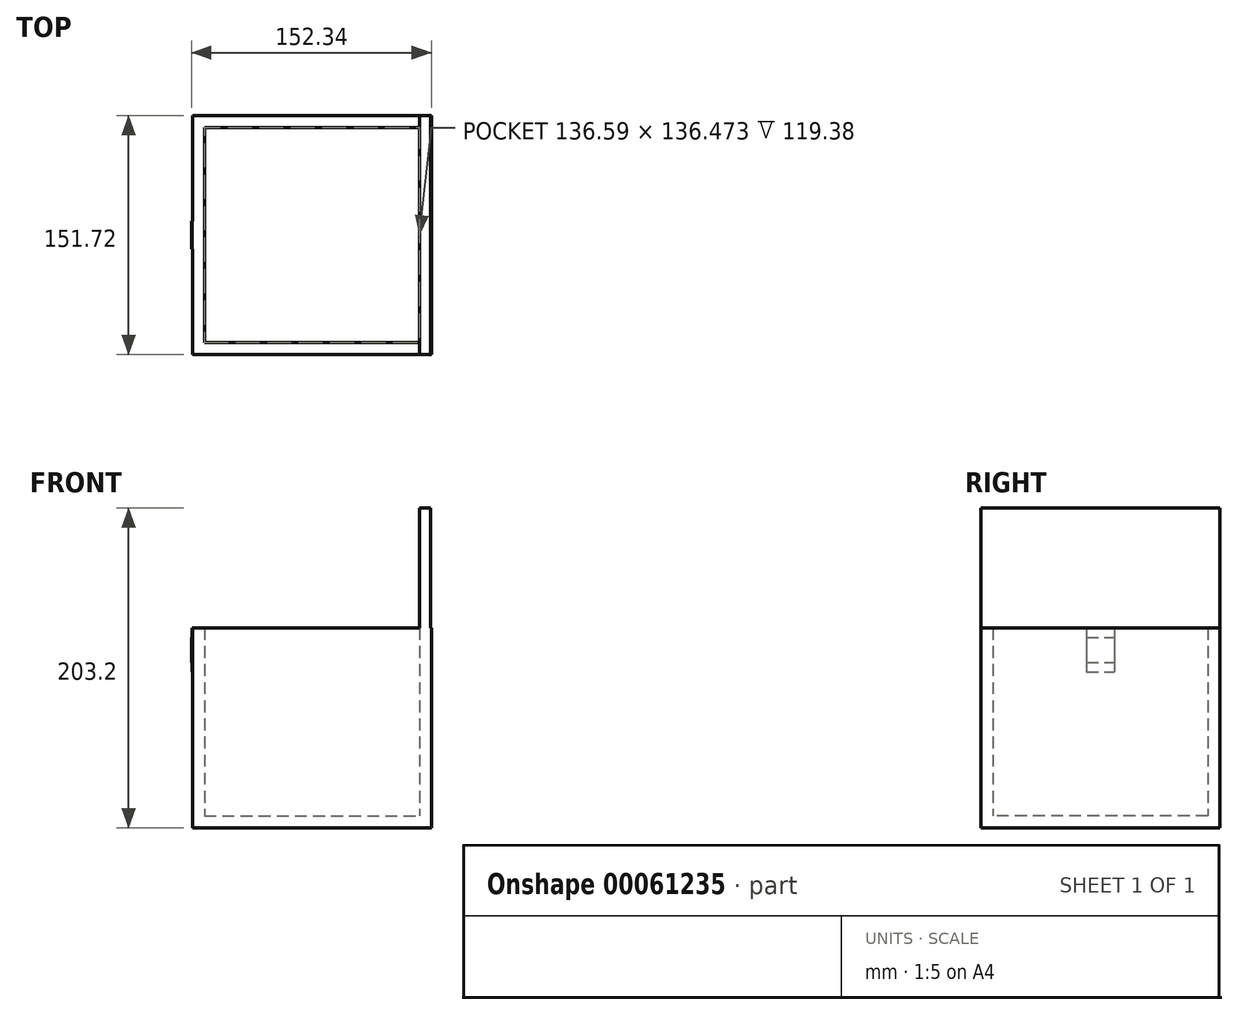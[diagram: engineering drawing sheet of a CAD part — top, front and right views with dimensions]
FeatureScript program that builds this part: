
annotation { "Feature Type Name" : "Feature", "Feature Type Description" : "" }
export const myFeature = defineFeature(function(context is Context, id is Id, definition is map)
    precondition{}
    {
        {
            var Q0;
            Q0=qCreatedBy(makeId("Top.planeOp"),FACE);
            var sketch = newSketch(context, id + "F0", { "sketchPlane" : qUnion([Q0])});
            skLineSegment(sketch, "E0.rect.bottom", {"start": v(-75.92, 75.86) * mm, "end": v(75.92, 75.86) * mm});
            skLineSegment(sketch, "E0.rect.top", {"start": v(-75.92, -75.86) * mm, "end": v(75.92, -75.86) * mm});
            skLineSegment(sketch, "E0.rect.left", {"start": v(-75.92, 75.86) * mm, "end": v(-75.92, -75.86) * mm});
            skLineSegment(sketch, "E0.rect.right", {"start": v(75.92, 75.86) * mm, "end": v(75.92, -75.86) * mm});
            skPoint(sketch, "E0.rect.middle", {"position": v(0, 0) * mm});
            skSolve(sketch);
        }
        {
            var Q0;
            Q0=makeQuery(id+"F0.imprint","IMPRINT",FACE,{"disambiguationData":[TD([[makeQuery(id+"F0.imprint","IMPRINT",EDGE,{"derivedFrom":sQuery(id+"F0.wireOp",EDGE,"E0.rect.bottom")}),-1.0]])]});
            extrude(context, id + "F1", {"entities" : qUnion([Q0]), "depth" : 127 * mm});
        }
        {
            var Q0;
            Q0=makeQuery(id+"F1.opExtrude","CAP_FACE",FACE,{"disambiguationData":[OSD([sQuery(id+"F0.wireOp",EDGE,"E0.rect.bottom"),sQuery(id+"F0.wireOp",EDGE,"E0.rect.top"),sQuery(id+"F0.wireOp",EDGE,"E0.rect.left"),sQuery(id+"F0.wireOp",EDGE,"E0.rect.right")])],"isStart":false});
            shell(context, id + "F2", {"entities" : qUnion([Q0]), "thickness" : 7.62 * mm});
        }
        {
            var Q0;
            Q0=makeQuery(id+"F1.opExtrude","CAP_FACE",FACE,{"disambiguationData":[OSD([sQuery(id+"F0.wireOp",EDGE,"E0.rect.bottom"),sQuery(id+"F0.wireOp",EDGE,"E0.rect.top"),sQuery(id+"F0.wireOp",EDGE,"E0.rect.left"),sQuery(id+"F0.wireOp",EDGE,"E0.rect.right")])],"isStart":false});
            var sketch = newSketch(context, id + "F3", { "sketchPlane" : qUnion([Q0])});
            skLineSegment(sketch, "E1.rect.bottom", {"start": v(75.24, -75.86) * mm, "end": v(68.36, -75.86) * mm});
            skLineSegment(sketch, "E1.rect.top", {"start": v(75.24, 83.18) * mm, "end": v(68.36, 83.18) * mm});
            skLineSegment(sketch, "E1.rect.left", {"start": v(75.24, -75.86) * mm, "end": v(75.24, 83.18) * mm});
            skLineSegment(sketch, "E1.rect.right", {"start": v(68.36, -75.86) * mm, "end": v(68.36, 83.18) * mm});
            skPoint(sketch, "E1.rect.middle", {"position": v(71.8, 3.66) * mm});
            skSolve(sketch);
        }
        {
            var Q0;
            {var subQ0=sQuery(id+"F3.wireOp",EDGE,"E1.rect.bottom");Q0=makeQuery(id+"F3.imprint","IMPRINT",FACE,{"disambiguationData":[TD([[makeQuery(id+"F3.imprint","IMPRINT",EDGE,{"derivedFrom":subQ0}),1.0]])]});}
            extrude(context, id + "F4", {"entities" : qUnion([Q0]), "operationType" : NewBodyOperationType.ADD, "depth" : 76.2 * mm});
        }
        {
            var Q0;
            Q0=makeQuery(id+"F1.opExtrude","SWEPT_FACE",FACE,{"disambiguationData":[OSD([sQuery(id+"F0.wireOp",EDGE,"E0.rect.left")])]});
            var sketch = newSketch(context, id + "F5", { "sketchPlane" : qUnion([Q0])});
            skLineSegment(sketch, "E2.rect.bottom", {"start": v(8.82, 127) * mm, "end": v(-8.82, 127) * mm});
            skLineSegment(sketch, "E2.rect.top", {"start": v(8.82, 99.04) * mm, "end": v(-8.82, 99.04) * mm});
            skLineSegment(sketch, "E2.rect.left", {"start": v(8.82, 127) * mm, "end": v(8.82, 99.04) * mm});
            skLineSegment(sketch, "E2.rect.right", {"start": v(-8.82, 127) * mm, "end": v(-8.82, 99.04) * mm});
            skPoint(sketch, "E2.rect.middle", {"position": v(0, 113.02) * mm});
            skPoint(sketch, "E2.rect.middle.positionSnap0", {"position": v(0, 127) * mm});
            skPoint(sketch, "E2.rect.centerSnap0", {"position": v(0, 127) * mm});
            skSolve(sketch);
        }
        {
            var Q0;
            Q0=makeQuery(id+"F5.imprint","IMPRINT",FACE,{"disambiguationData":[TD([[makeQuery(id+"F5.imprint","IMPRINT",EDGE,{"derivedFrom":sQuery(id+"F5.wireOp",EDGE,"E2.rect.bottom")}),-1.0]])]});
            extrude(context, id + "F6", {"entities" : qUnion([Q0]), "operationType" : NewBodyOperationType.ADD, "depth" : 0.25 * mm});
        }
        {
            var Q0;
            Q0=makeQuery(id+"F6.opExtrude","CAP_FACE",FACE,{"disambiguationData":[OSD([sQuery(id+"F5.wireOp",EDGE,"E2.rect.bottom"),sQuery(id+"F5.wireOp",EDGE,"E2.rect.top"),sQuery(id+"F5.wireOp",EDGE,"E2.rect.left"),sQuery(id+"F5.wireOp",EDGE,"E2.rect.right")])],"isStart":false});
            var sketch = newSketch(context, id + "F7", { "sketchPlane" : qUnion([Q0])});
            skLineSegment(sketch, "E3.rect.bottom", {"start": v(8.82, 120.84) * mm, "end": v(-8.82, 120.84) * mm});
            skLineSegment(sketch, "E3.rect.top", {"start": v(8.82, 105.2) * mm, "end": v(-8.82, 105.2) * mm});
            skLineSegment(sketch, "E3.rect.left", {"start": v(8.82, 120.84) * mm, "end": v(8.82, 105.2) * mm});
            skLineSegment(sketch, "E3.rect.right", {"start": v(-8.82, 120.84) * mm, "end": v(-8.82, 105.2) * mm});
            skPoint(sketch, "E3.rect.middle", {"position": v(0, 113.02) * mm});
            skPoint(sketch, "E3.rect.middle.positionSnap0", {"position": v(8.82, 113.02) * mm});
            skPoint(sketch, "E3.rect.centerSnap0", {"position": v(8.82, 113.02) * mm});
            skSolve(sketch);
        }
        {
            var Q0;
            Q0=makeQuery(id+"F7.imprint","IMPRINT",FACE,{"disambiguationData":[TD([[makeQuery(id+"F7.imprint","IMPRINT",EDGE,{"derivedFrom":sQuery(id+"F7.wireOp",EDGE,"E3.rect.bottom")}),1.0]])]});
            extrude(context, id + "F8", {"entities" : qUnion([Q0]), "operationType" : NewBodyOperationType.ADD, "depth" : 0.25 * mm});
        }
    });
